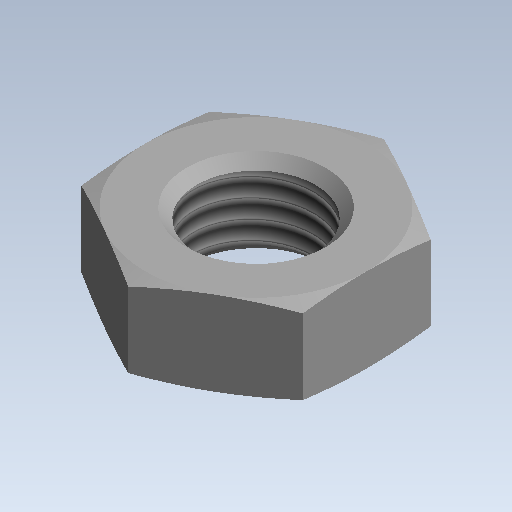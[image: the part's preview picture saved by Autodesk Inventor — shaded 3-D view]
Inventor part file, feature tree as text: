
AUTODESK INVENTOR PART (.ipt)
format: ipt  version: 2020 (Build 240168000, 168)  size: 156,672 bytes
history: native  units: mm (DEFAULTED — no unit token found)
features: other x70, sketch x3, revolve x2, extrude x1, thread x1
ambient origin geometry x8: Origin, YZ Plane, XZ Plane, XY Plane, X Axis, Y Axis, Z Axis, Center Point
bodies: Solid1 (feature_tree)
feature tree (77):
  sketch  "Sketch_8"  dims[d0=360.0deg d1=4.826mm d2=0.0mm]
  sketch  "Sketch_10"  dims[d3=360.0deg d4=3.68046mm d5=0.0mm]
  revolve  "Revolution1"  [1 undecoded]
  extrude  "Extrusion1"  Depth=3.68046mm TaperAngle=0.0deg
  revolve  "Revolution2"  [1 undecoded]
  thread  "Thread1"  [1 undecoded]
  other  "NUT_XY"
  other  "NUT_YZ"
  other  "NUT_ZX"
  other  "NUT_X"
  other  "NUT_Y"
  other  "NUT_Z"
  other  "NUT_Center"
  other  "a1_XY"
  other  "a1_YZ"
  other  "a1_ZX"
  other  "a1_X"
  other  "a1_Y"
  other  "a1_Z"
  other  "a1_Center"
  other  "a2_XY"
  other  "a2_YZ"
  other  "a2_ZX"
  other  "a2_X"
  other  "a2_Y"
  other  "a2_Z"
  other  "a2_Center"
  other  "b1_XY"
  other  "b1_YZ"
  other  "b1_ZX"
  other  "b1_X"
  other  "b1_Y"
  other  "b1_Z"
  other  "b1_Center"
  other  "b2_XY"
  other  "b2_YZ"
  other  "b2_ZX"
  other  "b2_X"
  other  "b2_Y"
  other  "b2_Z"
  other  "b2_Center"
  other  "e_XY"
  other  "e_YZ"
  other  "e_ZX"
  other  "e_X"
  other  "e_Y"
  other  "e_Z"
  other  "e_Center"
  other  "ol1_XY"
  other  "ol1_YZ"
  other  "ol1_ZX"
  other  "ol1_X"
  other  "ol1_Y"
  other  "ol1_Z"
  other  "ol1_Center"
  other  "ol2_XY"
  other  "ol2_YZ"
  other  "ol2_ZX"
  other  "ol2_X"
  other  "ol2_Y"
  other  "ol2_Z"
  other  "ol2_Center"
  other  "th1_XY"
  other  "th1_YZ"
  other  "th1_ZX"
  other  "th1_X"
  other  "th1_Y"
  other  "th1_Z"
  other  "th1_Center"
  other  "th2_XY"
  other  "th2_YZ"
  other  "th2_ZX"
  other  "th2_X"
  other  "th2_Y"
  other  "th2_Z"
  other  "th2_Center"
  sketch  "Sketch_11"  dims[d6=0.0mm d7=0.0mm d8=0.0mm]
note: 3 required parameter values undecoded (feature->parameter linkage not recoverable at this tier; creation-order binding heuristic only, values carry confidence <= 0.55)